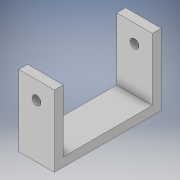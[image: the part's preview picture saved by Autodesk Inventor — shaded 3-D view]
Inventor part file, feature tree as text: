
AUTODESK INVENTOR PART (.ipt)
format: ipt  version: 2017 (Build 210142000, 142)  size: 111,616 bytes
history: native  units: in
note: dims shown in document units (in); Inventor stores cm internally (conversion verified against a paired STEP export)
features: sketch x2, extrude x1, hole x1, projected_geometry x1
ambient origin geometry x8: Origin, YZ Plane, XZ Plane, XY Plane, X Axis, Y Axis, Z Axis, Center Point
bodies: Solid1 (feature_tree)
feature tree (5):
  extrude  "Extrusion1"  Depth=3.0in
  hole  "Hole1"  [1 undecoded]
  sketch  "Sketch1"  dims[d0=2.0in d1=3.0in]
  sketch  "Sketch2"  dims[d2=0.25in d3=0.25in d4=0.25in d5=1.0in d6=0.0in d7=0.5in d8=0.5in d9=0.25in d10=0.75in d11=0.375in d12=0.25in d13=0.5635in d14=1.0in d15=0.8108in]
  projected_geometry  "Projected Loop1"
note: 1 required parameter value undecoded (feature->parameter linkage not recoverable at this tier; creation-order binding heuristic only, values carry confidence <= 0.55)
